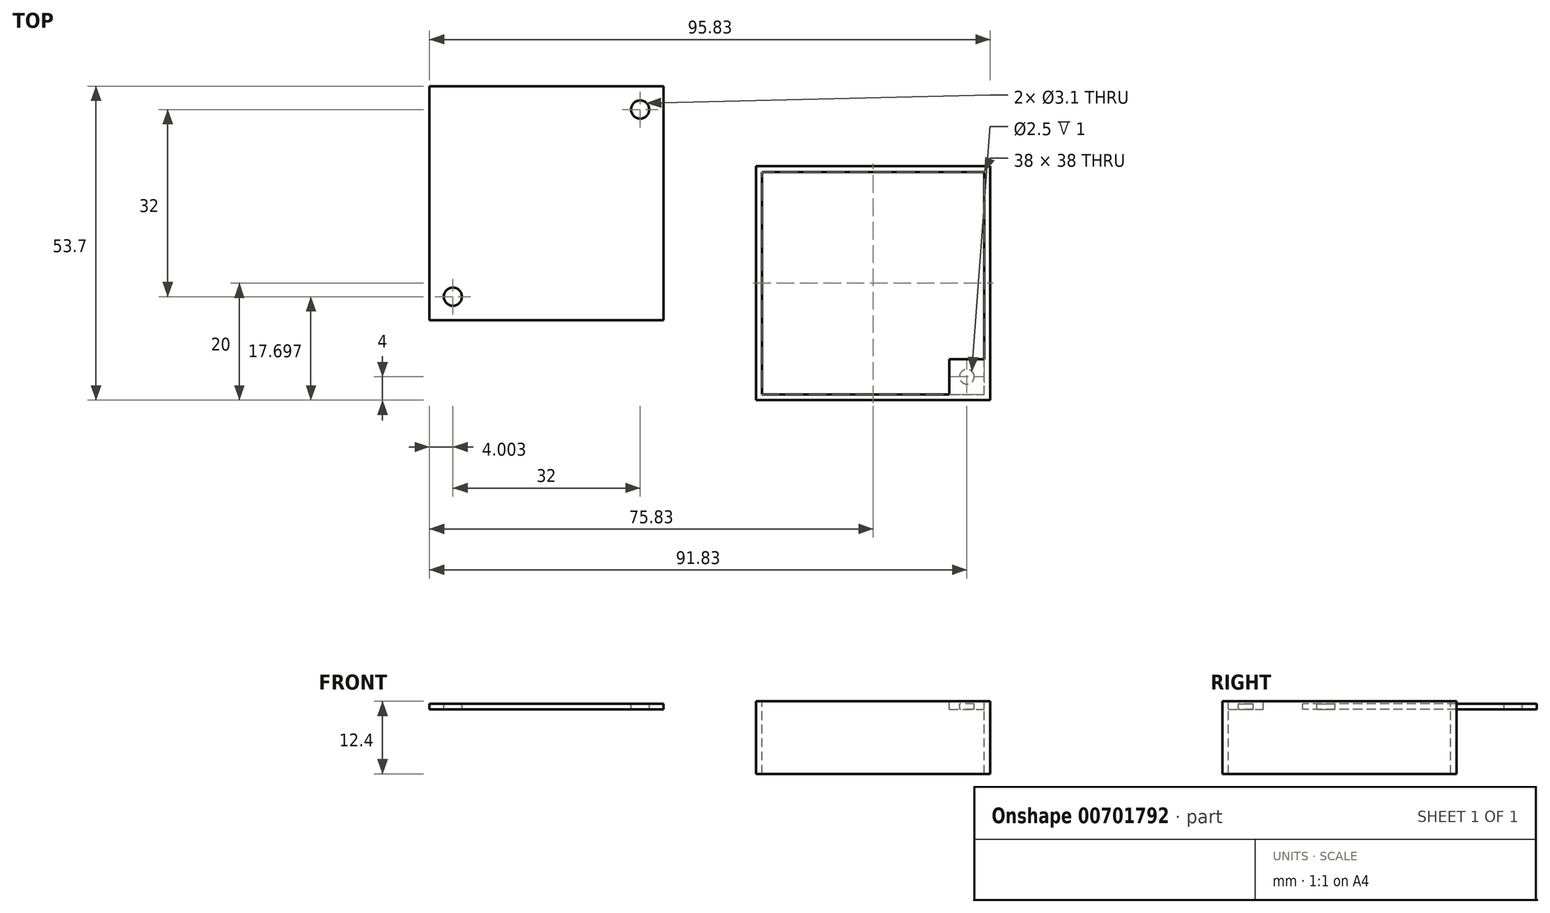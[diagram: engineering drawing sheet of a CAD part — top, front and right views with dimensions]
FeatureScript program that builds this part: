
annotation { "Feature Type Name" : "Feature", "Feature Type Description" : "" }
export const myFeature = defineFeature(function(context is Context, id is Id, definition is map)
    precondition{}
    {
        {
            var Q0;
            Q0=qCreatedBy(makeId("Top.planeOp"),FACE);
            var sketch = newSketch(context, id + "F0", { "sketchPlane" : qUnion([Q0])});
            skLineSegment(sketch, "E0.bottom", {"start": v(0, 0) * mm, "end": v(40, 0) * mm});
            skLineSegment(sketch, "E0.top", {"start": v(0, 40) * mm, "end": v(40, 40) * mm});
            skLineSegment(sketch, "E0.left", {"start": v(0, 0) * mm, "end": v(0, 40) * mm});
            skLineSegment(sketch, "E0.right", {"start": v(40, 0) * mm, "end": v(40, 40) * mm});
            skLineSegment(sketch, "E1.bottom", {"start": v(1, 1) * mm, "end": v(39, 1) * mm});
            skLineSegment(sketch, "E1.top", {"start": v(1, 39) * mm, "end": v(39, 39) * mm});
            skLineSegment(sketch, "E1.left", {"start": v(1, 1) * mm, "end": v(1, 39) * mm});
            skLineSegment(sketch, "E1.right", {"start": v(39, 1) * mm, "end": v(39, 39) * mm});
            skLineSegment(sketch, "E2.bottom", {"start": v(39, 1) * mm, "end": v(33, 1) * mm});
            skLineSegment(sketch, "E2.top", {"start": v(39, 7) * mm, "end": v(33, 7) * mm});
            skLineSegment(sketch, "E2.left", {"start": v(39, 1) * mm, "end": v(39, 7) * mm});
            skLineSegment(sketch, "E2.right", {"start": v(33, 1) * mm, "end": v(33, 7) * mm});
            skLineSegment(sketch, "E3.bottom", {"start": v(1, 39) * mm, "end": v(7, 39) * mm});
            skLineSegment(sketch, "E3.top", {"start": v(1, 33) * mm, "end": v(7, 33) * mm});
            skLineSegment(sketch, "E3.left", {"start": v(1, 39) * mm, "end": v(1, 33) * mm});
            skLineSegment(sketch, "E3.right", {"start": v(7, 39) * mm, "end": v(7, 33) * mm});
            skSolve(sketch);
        }
        {
            var Q0;
            Q0=qCreatedBy(makeId("Top.planeOp"),FACE);
            var sketch = newSketch(context, id + "F1", { "sketchPlane" : qUnion([Q0])});
            skCircle(sketch, "E4", {"center": v(8, 16.5) * mm, "radius": 1 * mm});
            skCircle(sketch, "E5", {"center": v(13, 16.5) * mm, "radius": 1 * mm});
            skCircle(sketch, "E6", {"center": v(8, 4.5) * mm, "radius": 1 * mm});
            skCircle(sketch, "E7", {"center": v(13, 4.5) * mm, "radius": 1 * mm});
            skPoint(sketch, "E8", {"position": v(10.5, 10.5) * mm});
            skCircle(sketch, "E9", {"center": v(8, 35.5) * mm, "radius": 1 * mm});
            skCircle(sketch, "E10", {"center": v(13, 35.5) * mm, "radius": 1 * mm});
            skCircle(sketch, "E11", {"center": v(8, 23.5) * mm, "radius": 1 * mm});
            skCircle(sketch, "E12", {"center": v(13, 23.5) * mm, "radius": 1 * mm});
            skPoint(sketch, "E13", {"position": v(10.5, 29.5) * mm});
            skCircle(sketch, "E14", {"center": v(27, 35.5) * mm, "radius": 1 * mm});
            skCircle(sketch, "E15", {"center": v(32, 35.5) * mm, "radius": 1 * mm});
            skCircle(sketch, "E16", {"center": v(27, 23.5) * mm, "radius": 1 * mm});
            skCircle(sketch, "E17", {"center": v(32, 23.5) * mm, "radius": 1 * mm});
            skPoint(sketch, "E18", {"position": v(29.5, 29.5) * mm});
            skCircle(sketch, "E19", {"center": v(27, 16.5) * mm, "radius": 1 * mm});
            skCircle(sketch, "E20", {"center": v(32, 16.5) * mm, "radius": 1 * mm});
            skCircle(sketch, "E21", {"center": v(27, 4.5) * mm, "radius": 1 * mm});
            skCircle(sketch, "E22", {"center": v(32, 4.5) * mm, "radius": 1 * mm});
            skPoint(sketch, "E23", {"position": v(29.5, 10.5) * mm});
            skSolve(sketch);
        }
        {
            var Q0;
            Q0=makeQuery(id+"F0.imprint","IMPRINT",FACE,{"disambiguationData":[TD([[makeQuery(id+"F0.imprint","IMPRINT",EDGE,{"derivedFrom":sQuery(id+"F0.wireOp",EDGE,"E0.bottom")}),1.0]])]});
            var Q1;
            Q1=makeQuery(id+"F0.imprint","IMPRINT",FACE,{"disambiguationData":[TD([[makeQuery(id+"F0.imprint","IMPRINT",EDGE,{"derivedFrom":sQuery(id+"F0.wireOp",EDGE,"E2.bottom")}),-1.0]])]});
            var Q2;
            Q2=makeQuery(id+"F0.imprint","IMPRINT",FACE,{"disambiguationData":[TD([[makeQuery(id+"F0.imprint","IMPRINT",EDGE,{"derivedFrom":sQuery(id+"F0.wireOp",EDGE,"E3.bottom")}),-1.0]])]});
            extrude(context, id + "F2", {"entities" : qUnion([Q0, Q1, Q2]), "depth" : -12 * mm, "offsetDistance" : 25 * mm});
        }
        {
            var Q0;
            Q0=makeQuery(id+"F0.imprint","IMPRINT",FACE,{"disambiguationData":[TD([[makeQuery(id+"F0.imprint","IMPRINT",EDGE,{"derivedFrom":sQuery(id+"F0.wireOp",EDGE,"E1.bottom")}),1.0]])]});
            extrude(context, id + "F3", {"entities" : qUnion([Q0]), "operationType" : NewBodyOperationType.ADD, "depth" : -1 * mm, "offsetDistance" : 25 * mm});
        }
        {
            var Q0;
            Q0 = qSketchRegion(id + "F1", true);
            extrude(context, id + "F4", {"entities" : qUnion([Q0]), "operationType" : NewBodyOperationType.REMOVE, "depth" : -2 * mm, "offsetDistance" : 25 * mm});
        }
        {
            var Q0;
            Q0=makeQuery(id+"F0.imprint","IMPRINT",FACE,{"disambiguationData":[TD([[makeQuery(id+"F0.imprint","IMPRINT",EDGE,{"derivedFrom":sQuery(id+"F0.wireOp",EDGE,"E1.bottom")}),1.0]])]});
            var sketch = newSketch(context, id + "F5", { "sketchPlane" : qUnion([Q0])});
            skCircle(sketch, "E24", {"center": v(36, 4) * mm, "radius": 1.25 * mm});
            skCircle(sketch, "E25", {"center": v(4, 36) * mm, "radius": 1.25 * mm});
            skSolve(sketch);
        }
        {
            var Q0;
            Q0 = qSketchRegion(id + "F5", true);
            extrude(context, id + "F6", {"entities" : qUnion([Q0]), "operationType" : NewBodyOperationType.REMOVE, "oppositeDirection" : true, "depth" : 25 * mm, "offsetDistance" : 25 * mm});
        }
        {
            var Q0;
            Q0=makeQuery(id+"F0.imprint","IMPRINT",FACE,{"disambiguationData":[TD([[makeQuery(id+"F0.imprint","IMPRINT",EDGE,{"derivedFrom":sQuery(id+"F0.wireOp",EDGE,"E0.bottom")}),1.0]])]});
            var Q1;
            Q1=makeQuery(id+"F0.imprint","IMPRINT",FACE,{"disambiguationData":[TD([[makeQuery(id+"F0.imprint","IMPRINT",EDGE,{"derivedFrom":sQuery(id+"F0.wireOp",EDGE,"E1.bottom")}),1.0]])]});
            var Q2;
            Q2=makeQuery(id+"F0.imprint","IMPRINT",FACE,{"disambiguationData":[TD([[makeQuery(id+"F0.imprint","IMPRINT",EDGE,{"derivedFrom":sQuery(id+"F0.wireOp",EDGE,"E2.bottom")}),-1.0]])]});
            var Q3;
            Q3=makeQuery(id+"F0.imprint","IMPRINT",FACE,{"disambiguationData":[TD([[makeQuery(id+"F0.imprint","IMPRINT",EDGE,{"derivedFrom":sQuery(id+"F0.wireOp",EDGE,"E3.bottom")}),-1.0]])]});
            extrude(context, id + "F7", {"entities" : qUnion([Q0, Q1, Q2, Q3]), "operationType" : NewBodyOperationType.ADD, "depth" : 0.4 * mm, "offsetDistance" : 25 * mm});
        }
        {
            var Q0;
            Q0=qCreatedBy(makeId("Top.planeOp"),FACE);
            var sketch = newSketch(context, id + "F8", { "sketchPlane" : qUnion([Q0])});
            skLineSegment(sketch, "E26.bottom", {"start": v(-15.83, 53.7) * mm, "end": v(-55.83, 53.7) * mm});
            skLineSegment(sketch, "E26.top", {"start": v(-15.83, 13.7) * mm, "end": v(-55.83, 13.7) * mm});
            skLineSegment(sketch, "E26.left", {"start": v(-15.83, 53.7) * mm, "end": v(-15.83, 13.7) * mm});
            skLineSegment(sketch, "E26.right", {"start": v(-55.83, 53.7) * mm, "end": v(-55.83, 13.7) * mm});
            skCircle(sketch, "E27", {"center": v(-19.83, 49.7) * mm, "radius": 1.55 * mm});
            skCircle(sketch, "E28", {"center": v(-51.83, 17.7) * mm, "radius": 1.55 * mm});
            skSolve(sketch);
        }
        {
            var Q0;
            Q0=makeQuery(id+"F8.imprint","IMPRINT",FACE,{"disambiguationData":[TD([[makeQuery(id+"F8.imprint","IMPRINT",EDGE,{"derivedFrom":sQuery(id+"F8.wireOp",EDGE,"E26.bottom")}),1.0]])]});
            extrude(context, id + "F9", {"entities" : qUnion([Q0]), "oppositeDirection" : true, "depth" : 1 * mm, "offsetDistance" : 25 * mm});
        }
    });
